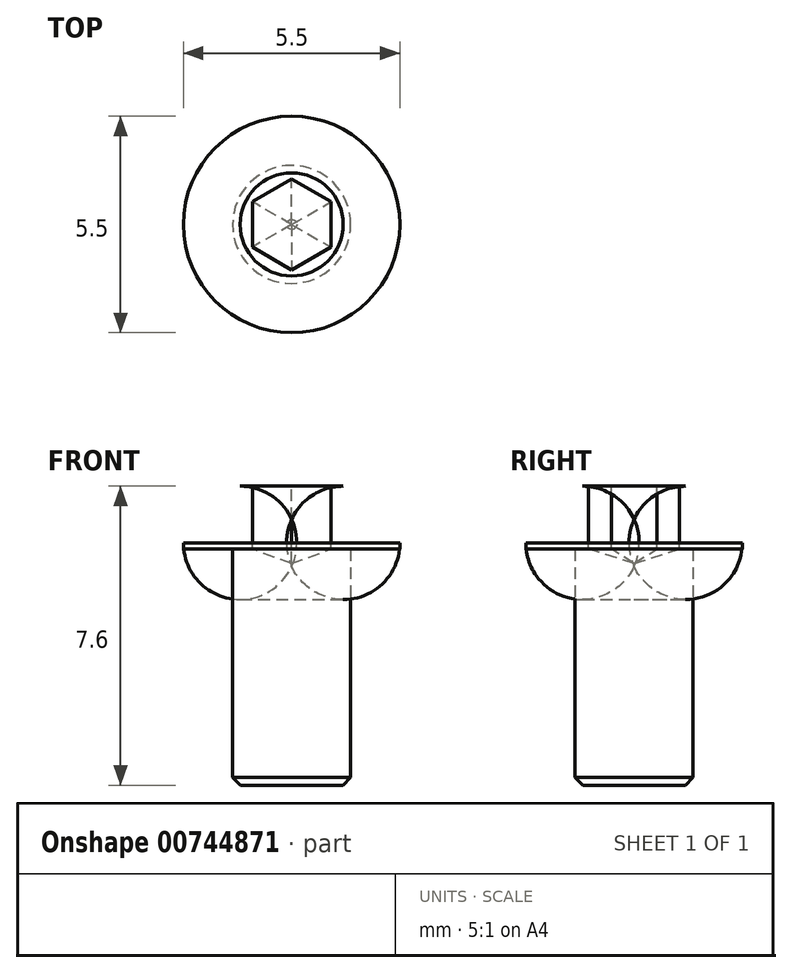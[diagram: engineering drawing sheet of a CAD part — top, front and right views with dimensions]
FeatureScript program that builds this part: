
annotation { "Feature Type Name" : "Feature", "Feature Type Description" : "" }
export const myFeature = defineFeature(function(context is Context, id is Id, definition is map)
    precondition{}
    {
        {
            var Q0;
            Q0=qCreatedBy(makeId("Front.planeOp"),FACE);
            var sketch = newSketch(context, id + "F0", { "sketchPlane" : qUnion([Q0])});
            skLineSegment(sketch, "E0", {"start": v(0, 0) * mm, "end": v(0, 7.52) * mm, "construction": true});
            skLineSegment(sketch, "E1", {"start": v(0, 0) * mm, "end": v(6.23, 0) * mm, "construction": true});
            skLineSegment(sketch, "E2", {"start": v(0, -6) * mm, "end": v(1.5, -6) * mm});
            skLineSegment(sketch, "E3", {"start": v(1.5, -6) * mm, "end": v(1.5, 0) * mm});
            skLineSegment(sketch, "E4", {"start": v(1.5, 0) * mm, "end": v(2.75, 0) * mm});
            skLineSegment(sketch, "E5", {"start": v(2.75, 0) * mm, "end": v(2.75, 0.16) * mm});
            skArc(sketch, "E6", {"start": v(2.75, 0.16) * mm, "mid": v(2.33, 1.18) * mm, "end": v(1.31, 1.6) * mm});
            skLineSegment(sketch, "E7", {"start": v(1.31, 1.6) * mm, "end": v(0, 1.6) * mm});
            skLineSegment(sketch, "E8", {"start": v(0, 1.6) * mm, "end": v(0, -6) * mm});
            skSolve(sketch);
        }
        {
            var Q0;
            Q0 = qSketchRegion(id + "F0", true);
            var Q1;
            Q1=sQuery(id+"F0.wireOp",EDGE,"E0");
            revolve(context, id + "F1", {"surfaceOperationType" : NewSurfaceOperationType.NEW, "entities" : qUnion([Q0]), "axis" : qUnion([Q1]), "revolveType" : RevolveType.FULL});
        }
        {
            var Q0;
            Q0=makeQuery(id+"F1.opRevolve","SWEPT_FACE",FACE,{"disambiguationData":[OSD([sQuery(id+"F0.wireOp",EDGE,"E7")])]});
            var sketch = newSketch(context, id + "F2", { "sketchPlane" : qUnion([Q0])});
            skCircle(sketch, "E9.cCircle", {"center": v(0, 0) * mm, "radius": 1 * mm, "construction": true});
            skLineSegment(sketch, "E9.0", {"start": v(-1, -0.58) * mm, "end": v(-1, 0.58) * mm});
            skLineSegment(sketch, "E9.1", {"start": v(-1, 0.58) * mm, "end": v(0, 1.15) * mm});
            skLineSegment(sketch, "E9.2", {"start": v(0, 1.15) * mm, "end": v(1, 0.58) * mm});
            skLineSegment(sketch, "E9.3", {"start": v(1, 0.58) * mm, "end": v(1, -0.58) * mm});
            skLineSegment(sketch, "E9.4", {"start": v(1, -0.58) * mm, "end": v(0, -1.15) * mm});
            skLineSegment(sketch, "E9.5", {"start": v(0, -1.15) * mm, "end": v(-1, -0.58) * mm});
            skPoint(sketch, "E9.0.midPoint", {"position": v(-1, 0) * mm});
            skSolve(sketch);
        }
        {
            var Q0;
            Q0 = qSketchRegion(id + "F2", true);
            extrude(context, id + "F3", {"entities" : qUnion([Q0]), "operationType" : NewBodyOperationType.REMOVE, "oppositeDirection" : true, "depth" : 1.6 * mm, "offsetDistance" : 25 * mm});
        }
        {
            var Q0;
            Q0=makeQuery(id+"F3.boolean.opBoolean","COPY",FACE,{"derivedFrom":makeQuery(id+"F3.opExtrude","CAP_FACE",FACE,{"disambiguationData":[OSD([sQuery(id+"F2.wireOp",EDGE,"E9.0"),sQuery(id+"F2.wireOp",EDGE,"E9.1"),sQuery(id+"F2.wireOp",EDGE,"E9.2"),sQuery(id+"F2.wireOp",EDGE,"E9.3"),sQuery(id+"F2.wireOp",EDGE,"E9.4"),sQuery(id+"F2.wireOp",EDGE,"E9.5")])],"isStart":false})});
            var sketch = newSketch(context, id + "F4", { "sketchPlane" : qUnion([Q0])});
            skLineSegment(sketch, "E10.0.0", {"start": v(-1, -0.58) * mm, "end": v(0, -1.15) * mm});
            skLineSegment(sketch, "E10.0.1", {"start": v(0, -1.15) * mm, "end": v(1, -0.58) * mm});
            skLineSegment(sketch, "E10.0.2", {"start": v(1, -0.58) * mm, "end": v(1, 0.58) * mm});
            skLineSegment(sketch, "E10.0.3", {"start": v(1, 0.58) * mm, "end": v(0, 1.15) * mm});
            skLineSegment(sketch, "E10.0.4", {"start": v(0, 1.15) * mm, "end": v(-1, 0.58) * mm});
            skLineSegment(sketch, "E10.0.5", {"start": v(-1, 0.58) * mm, "end": v(-1, -0.58) * mm});
            skSolve(sketch);
        }
        {
            var Q0;
            Q0 = qSketchRegion(id + "F4", true);
            extrude(context, id + "F5", {"entities" : qUnion([Q0]), "operationType" : NewBodyOperationType.REMOVE, "oppositeDirection" : true, "depth" : 25 * mm, "offsetDistance" : 25 * mm, "hasDraft" : true, "draftAngle" : 70 * degree, "draftPullDirection" : true});
        }
        {
            var Q0;
            Q0=makeQuery(id+"F1.opRevolve","SWEPT_EDGE",EDGE,{"disambiguationData":[OSD([sQuery(id+"F0.wireOp",EDGE,"E2"),sQuery(id+"F0.wireOp",EDGE,"E3")])]});
            chamfer(context, id + "F6", {"entities" : qUnion([Q0]), "width" : 0.2 * mm, "tangentPropagation" : true});
        }
    });
